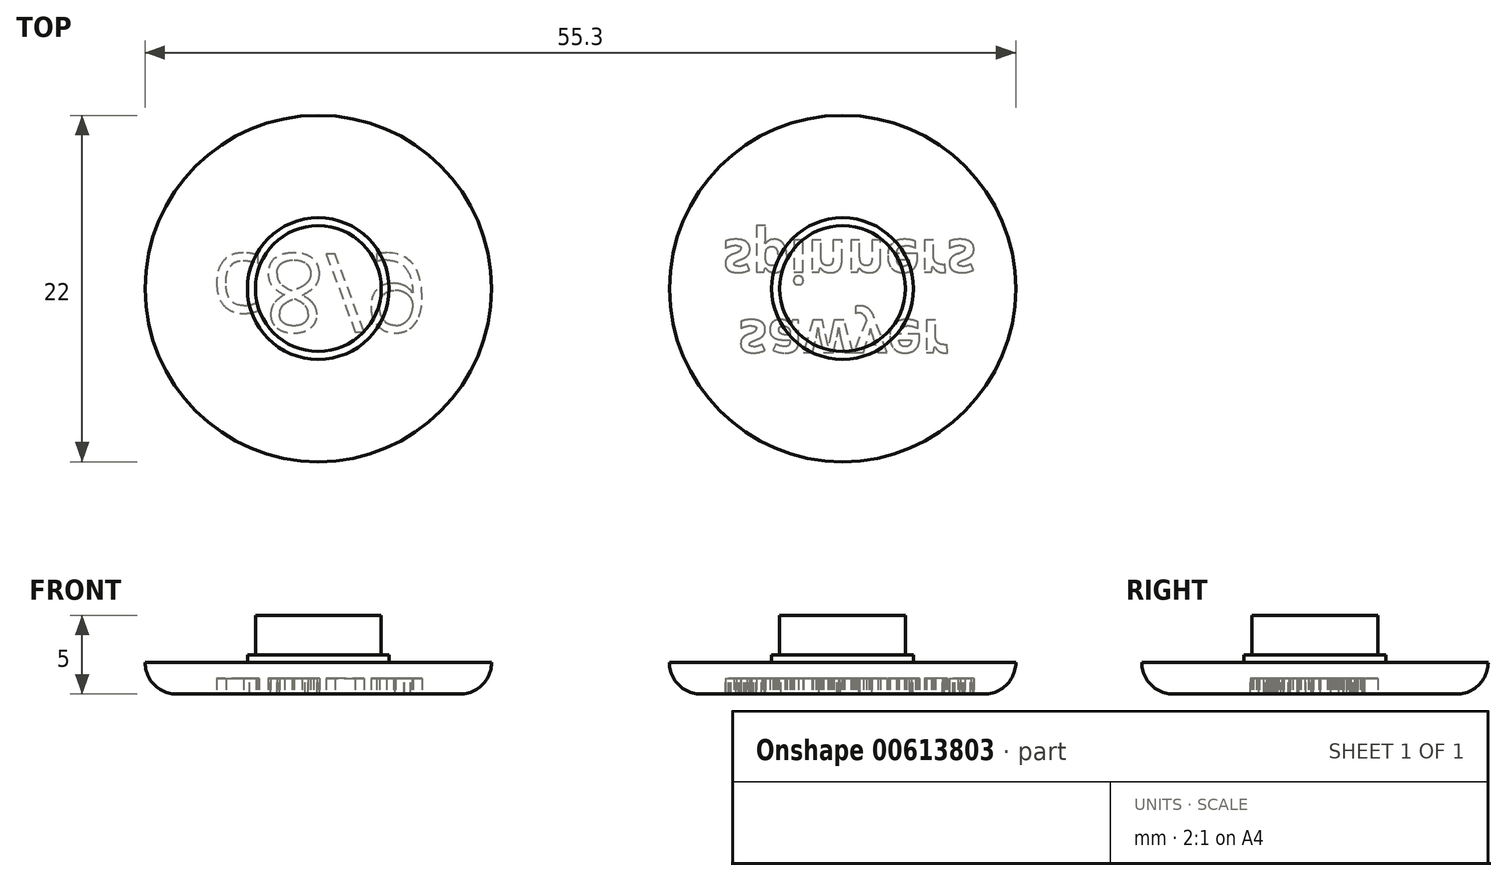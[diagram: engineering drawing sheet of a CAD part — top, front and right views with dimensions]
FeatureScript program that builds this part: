
annotation { "Feature Type Name" : "Feature", "Feature Type Description" : "" }
export const myFeature = defineFeature(function(context is Context, id is Id, definition is map)
    precondition{}
    {
        {
            var Q0;
            Q0=qCreatedBy(makeId("Top.planeOp"),FACE);
            var sketch = newSketch(context, id + "F0", { "sketchPlane" : qUnion([Q0])});
            skCircle(sketch, "E0", {"center": v(-124.76, 13.61) * mm, "radius": 11 * mm});
            skSolve(sketch);
        }
        {
            var Q0;
            Q0=makeQuery(id+"F0.imprint","IMPRINT",FACE,{"disambiguationData":[TD([[makeQuery(id+"F0.imprint","IMPRINT",EDGE,{"derivedFrom":sQuery(id+"F0.wireOp",EDGE,"E0")}),1.0]])]});
            extrude(context, id + "F1", {"entities" : qUnion([Q0]), "depth" : 2 * mm, "offsetDistance" : 25 * mm});
        }
        {
            var Q0;
            Q0=makeQuery(id+"F1.opExtrude","CAP_FACE",FACE,{"disambiguationData":[OSD([sQuery(id+"F0.wireOp",EDGE,"E0")])],"isStart":false});
            var sketch = newSketch(context, id + "F2", { "sketchPlane" : qUnion([Q0])});
            skCircle(sketch, "E1", {"center": v(-124.76, 13.61) * mm, "radius": 4.5 * mm});
            skSolve(sketch);
        }
        {
            var Q0;
            Q0=makeQuery(id+"F2.imprint","IMPRINT",FACE,{"disambiguationData":[TD([[makeQuery(id+"F2.imprint","IMPRINT",EDGE,{"derivedFrom":sQuery(id+"F2.wireOp",EDGE,"E1")}),1.0]])]});
            extrude(context, id + "F3", {"entities" : qUnion([Q0]), "operationType" : NewBodyOperationType.ADD, "depth" : 0.5 * mm, "offsetDistance" : 25 * mm});
        }
        {
            var Q0;
            Q0=makeQuery(id+"F3.opExtrude","CAP_FACE",FACE,{"disambiguationData":[OSD([sQuery(id+"F2.wireOp",EDGE,"E1")])],"isStart":false});
            var sketch = newSketch(context, id + "F4", { "sketchPlane" : qUnion([Q0])});
            skCircle(sketch, "E2", {"center": v(-124.76, 13.61) * mm, "radius": 4 * mm});
            skSolve(sketch);
        }
        {
            var Q0;
            Q0=makeQuery(id+"F4.imprint","IMPRINT",FACE,{"disambiguationData":[TD([[makeQuery(id+"F4.imprint","IMPRINT",EDGE,{"derivedFrom":sQuery(id+"F4.wireOp",EDGE,"E2")}),1.0]])]});
            extrude(context, id + "F5", {"entities" : qUnion([Q0]), "operationType" : NewBodyOperationType.ADD, "depth" : 2.5 * mm, "offsetDistance" : 25 * mm});
        }
        {
            var Q0;
            Q0=makeQuery(id+"F1.opExtrude","CAP_EDGE",EDGE,{"disambiguationData":[OSD([sQuery(id+"F0.wireOp",EDGE,"E0")])],"isStart":true});
            var Q1;
            Q1=makeQuery(id+"F3.opExtrude","CAP_EDGE",EDGE,{"disambiguationData":[OSD([sQuery(id+"F2.wireOp",EDGE,"E1")])],"isStart":true});
            fillet(context, id + "F6", {"entities" : qUnion([Q0, Q1]), "radius" : 2 * mm, "tangentPropagation" : true, "allowEdgeOverflow" : false});
        }
        {
            var Q0;
            Q0=makeQuery(id+"F1.opExtrude","CAP_FACE",FACE,{"disambiguationData":[OSD([sQuery(id+"F0.wireOp",EDGE,"E0")])],"isStart":true});
            var sketch = newSketch(context, id + "F7", { "sketchPlane" : qUnion([Q0])});
            skText(sketch, "E3", { "text": "c8/9", "fontName": "OpenSans-Regular.ttf"});
            skPoint(sketch, "E3.secondSnap0", {"position": v(-117.72, -13.61) * mm});
            const initialGuessF7  = {"E3": [-0.1316, -0.01582, 1, 0, 0.005]};
            skSetInitialGuess(sketch, initialGuessF7);
            skSolve(sketch);
        }
        {
            var Q0;
            Q0=makeQuery(id+"F1.opExtrude","SWEPT_BODY",BODY,{"disambiguationData":[OSD([sQuery(id+"F0.wireOp",EDGE,"E0")])]});
            transform(context, id + "F8", {"entities" : qUnion([Q0]), "transformType" : TransformType.TRANSLATION_3D, "dx" : 33.3 * mm, "dy" : 0 * mm, "dz" : 0 * mm, "makeCopy" : true});
        }
        {
            var Q0;
            Q0=makeQuery(id+"F8.opPattern","COPY",FACE,{"derivedFrom":makeQuery(id+"F1.opExtrude","CAP_FACE",FACE,{"disambiguationData":[OSD([sQuery(id+"F0.wireOp",EDGE,"E0")])],"isStart":true}),"instanceName":"1"});
            var sketch = newSketch(context, id + "F9", { "sketchPlane" : qUnion([Q0])});
            skText(sketch, "E4", { "text": " sawyer\nspinners", "fontName": "OpenSans-Bold.ttf"});
            skPoint(sketch, "E4.secondSnap0", {"position": v(-82.88, -13.73) * mm});
            const initialGuessF9  = {"E4": [-0.09907, -0.01161, 1, 0, 0.0027]};
            skSetInitialGuess(sketch, initialGuessF9);
            skSolve(sketch);
        }
        {
            var Q0;
            Q0 = qSketchRegion(id + "F7", true);
            extrude(context, id + "F10", {"entities" : qUnion([Q0]), "operationType" : NewBodyOperationType.REMOVE, "oppositeDirection" : true, "depth" : 1 * mm, "offsetDistance" : 25 * mm});
        }
        {
            var Q0;
            Q0 = qSketchRegion(id + "F9", true);
            extrude(context, id + "F11", {"entities" : qUnion([Q0]), "operationType" : NewBodyOperationType.REMOVE, "oppositeDirection" : true, "depth" : 1 * mm, "offsetDistance" : 25 * mm});
        }
    });
